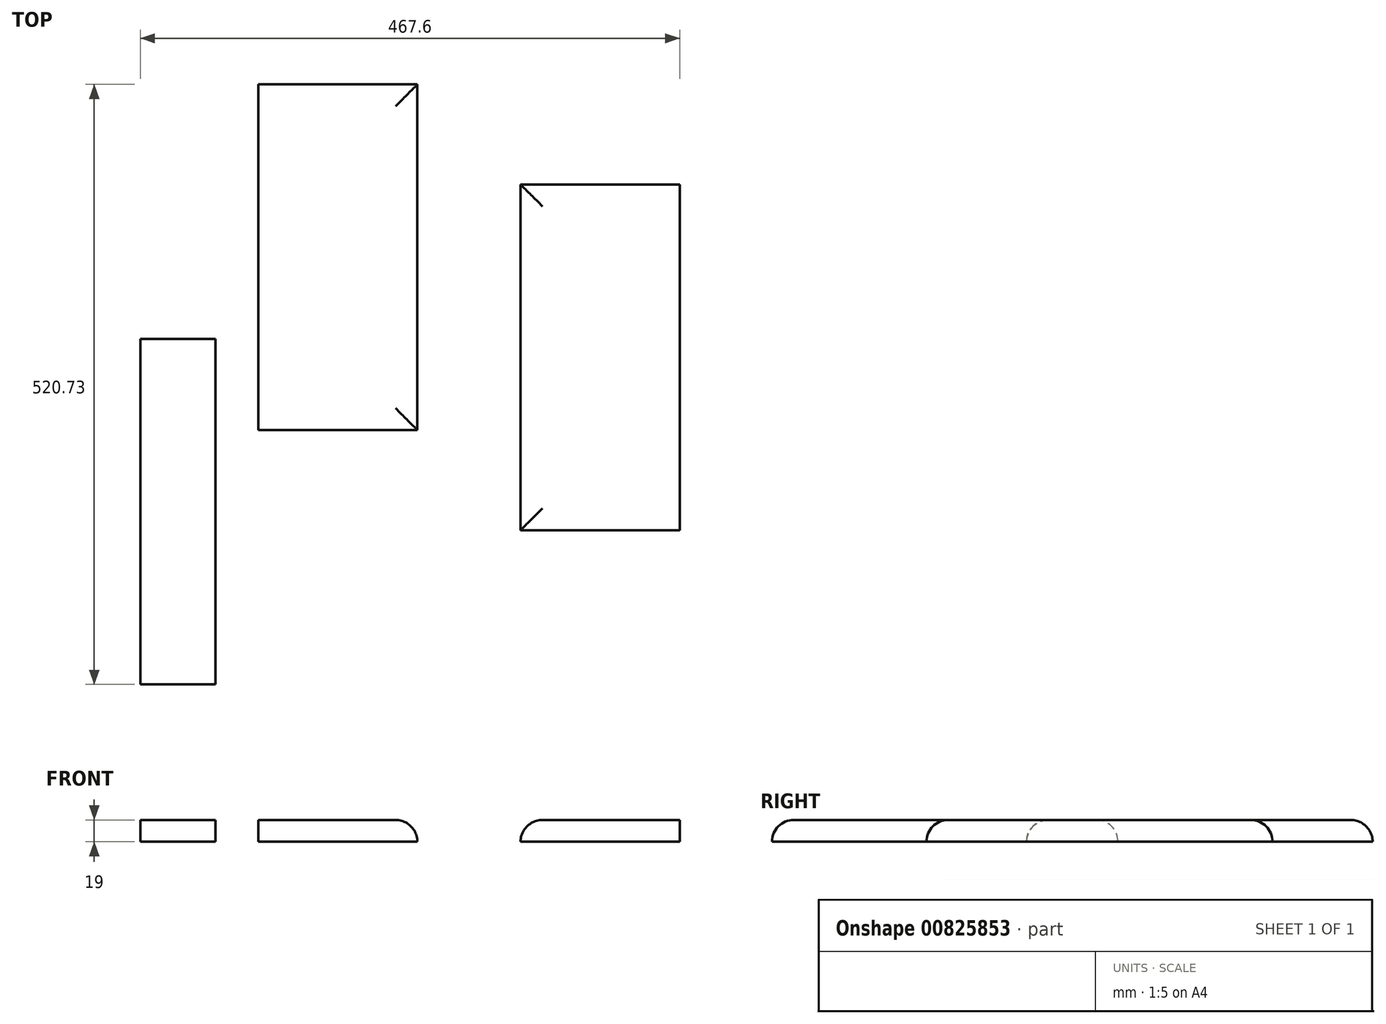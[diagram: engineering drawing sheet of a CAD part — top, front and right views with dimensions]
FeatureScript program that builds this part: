
annotation { "Feature Type Name" : "Feature", "Feature Type Description" : "" }
export const myFeature = defineFeature(function(context is Context, id is Id, definition is map)
    precondition{}
    {
        {
            var Q0;
            Q0=qCreatedBy(makeId("Top.planeOp"),FACE);
            var sketch = newSketch(context, id + "F0", { "sketchPlane" : qUnion([Q0])});
            skLineSegment(sketch, "E0.bottom", {"start": v(-146.23, 220.73) * mm, "end": v(-8.23, 220.73) * mm});
            skLineSegment(sketch, "E0.top", {"start": v(-146.23, -79.27) * mm, "end": v(-8.23, -79.27) * mm});
            skLineSegment(sketch, "E0.left", {"start": v(-146.23, 220.73) * mm, "end": v(-146.23, -79.27) * mm});
            skLineSegment(sketch, "E0.right", {"start": v(-8.23, 220.73) * mm, "end": v(-8.23, -79.27) * mm});
            skSolve(sketch);
        }
        {
            var Q0;
            Q0=makeQuery(id+"F0.imprint","IMPRINT",FACE,{"disambiguationData":[TD([[makeQuery(id+"F0.imprint","IMPRINT",EDGE,{"derivedFrom":sQuery(id+"F0.wireOp",EDGE,"E0.bottom")}),-1.0]])]});
            extrude(context, id + "F1", {"entities" : qUnion([Q0]), "depth" : 19 * mm, "offsetDistance" : 25 * mm});
        }
        {
            var Q0;
            Q0=qCreatedBy(makeId("Top.planeOp"),FACE);
            var sketch = newSketch(context, id + "F2", { "sketchPlane" : qUnion([Q0])});
            skLineSegment(sketch, "E1.bottom", {"start": v(-248.35, 0) * mm, "end": v(-183.35, 0) * mm});
            skLineSegment(sketch, "E1.top", {"start": v(-248.35, -300) * mm, "end": v(-183.35, -300) * mm});
            skLineSegment(sketch, "E1.left", {"start": v(-248.35, 0) * mm, "end": v(-248.35, -300) * mm});
            skLineSegment(sketch, "E1.right", {"start": v(-183.35, 0) * mm, "end": v(-183.35, -300) * mm});
            skSolve(sketch);
        }
        {
            var Q0;
            Q0 = qSketchRegion(id + "F2", true);
            extrude(context, id + "F3", {"entities" : qUnion([Q0]), "depth" : 19 * mm, "offsetDistance" : 25 * mm});
        }
        {
            var Q0;
            Q0=qCreatedBy(makeId("Top.planeOp"),FACE);
            var sketch = newSketch(context, id + "F4", { "sketchPlane" : qUnion([Q0])});
            skLineSegment(sketch, "E2.bottom", {"start": v(81.25, 133.92) * mm, "end": v(219.25, 133.92) * mm});
            skLineSegment(sketch, "E2.top", {"start": v(81.25, -166.08) * mm, "end": v(219.25, -166.08) * mm});
            skLineSegment(sketch, "E2.left", {"start": v(81.25, 133.92) * mm, "end": v(81.25, -166.08) * mm});
            skLineSegment(sketch, "E2.right", {"start": v(219.25, 133.92) * mm, "end": v(219.25, -166.08) * mm});
            skSolve(sketch);
        }
        {
            var Q0;
            Q0 = qSketchRegion(id + "F4", true);
            extrude(context, id + "F5", {"entities" : qUnion([Q0]), "depth" : 19 * mm, "offsetDistance" : 25 * mm});
        }
        {
            var Q0;
            Q0=makeQuery(id+"F3.opExtrude","CAP_EDGE",EDGE,{"disambiguationData":[OSD([sQuery(id+"F2.wireOp",EDGE,"E1.bottom")])],"isStart":false});
            var Q1;
            Q1=makeQuery(id+"F3.opExtrude","CAP_EDGE",EDGE,{"disambiguationData":[OSD([sQuery(id+"F2.wireOp",EDGE,"E1.top")])],"isStart":false});
            var Q2;
            Q2=makeQuery(id+"F1.opExtrude","CAP_EDGE",EDGE,{"disambiguationData":[OSD([sQuery(id+"F0.wireOp",EDGE,"E0.top")])],"isStart":false});
            var Q3;
            Q3=makeQuery(id+"F1.opExtrude","CAP_EDGE",EDGE,{"disambiguationData":[OSD([sQuery(id+"F0.wireOp",EDGE,"E0.right")])],"isStart":false});
            var Q4;
            Q4=makeQuery(id+"F1.opExtrude","CAP_EDGE",EDGE,{"disambiguationData":[OSD([sQuery(id+"F0.wireOp",EDGE,"E0.bottom")])],"isStart":false});
            var Q5;
            Q5=makeQuery(id+"F5.opExtrude","CAP_EDGE",EDGE,{"disambiguationData":[OSD([sQuery(id+"F4.wireOp",EDGE,"E2.bottom")])],"isStart":false});
            var Q6;
            Q6=makeQuery(id+"F5.opExtrude","CAP_EDGE",EDGE,{"disambiguationData":[OSD([sQuery(id+"F4.wireOp",EDGE,"E2.left")])],"isStart":false});
            var Q7;
            Q7=makeQuery(id+"F5.opExtrude","CAP_EDGE",EDGE,{"disambiguationData":[OSD([sQuery(id+"F4.wireOp",EDGE,"E2.top")])],"isStart":false});
            fillet(context, id + "F6", {"entities" : qUnion([Q0, Q1, Q2, Q3, Q4, Q5, Q6, Q7]), "radius" : 19 * mm, "tangentPropagation" : true, "allowEdgeOverflow" : false});
        }
    });
